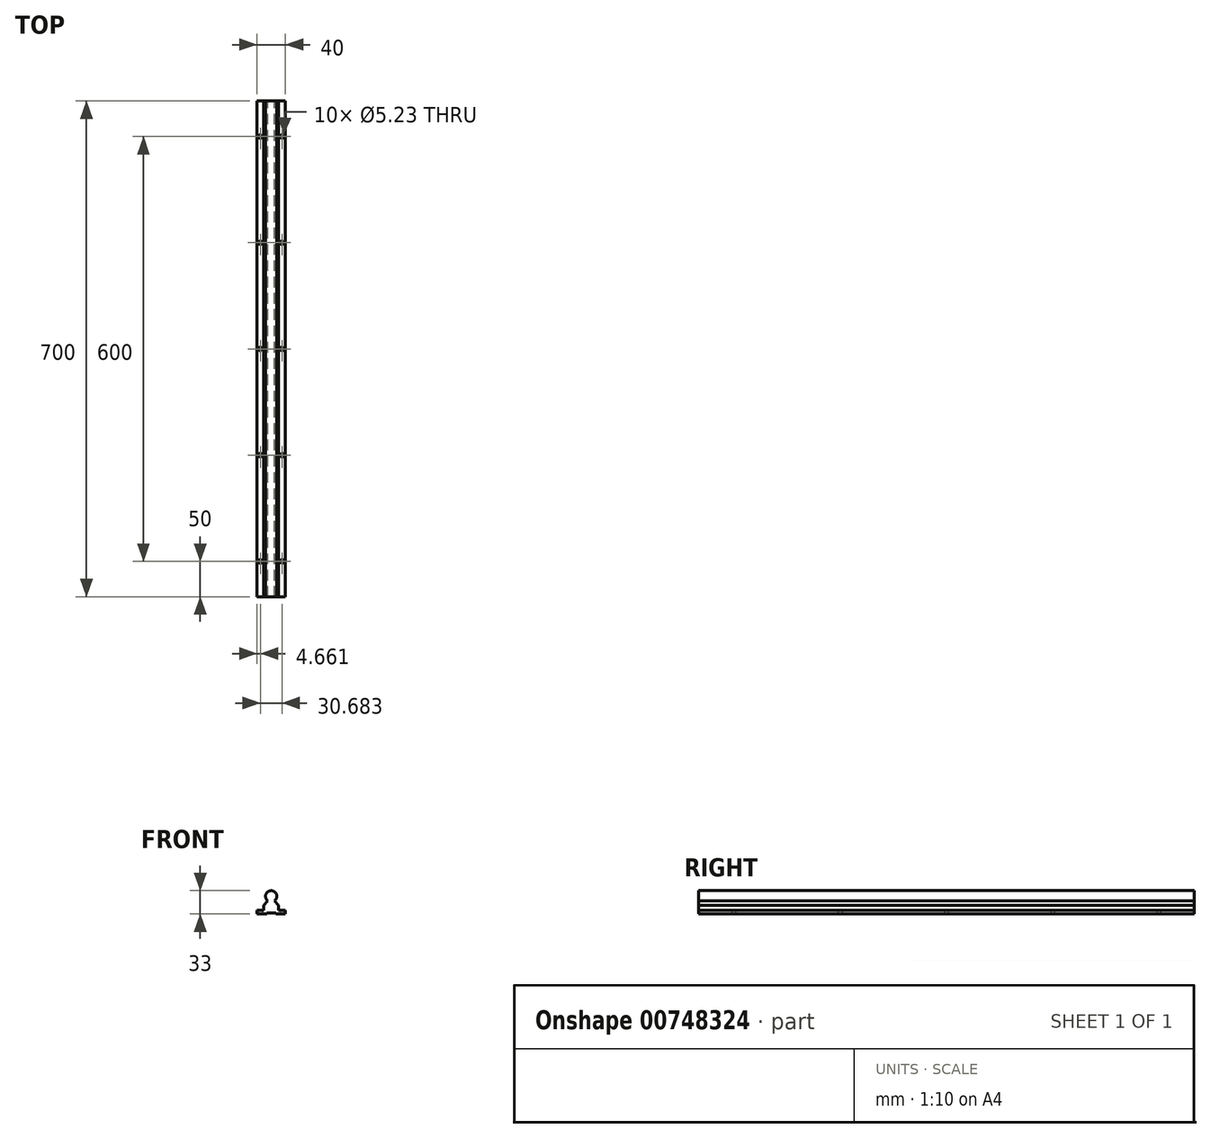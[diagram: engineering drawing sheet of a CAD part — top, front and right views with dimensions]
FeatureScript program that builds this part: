
annotation { "Feature Type Name" : "Feature", "Feature Type Description" : "" }
export const myFeature = defineFeature(function(context is Context, id is Id, definition is map)
    precondition{}
    {
        {
            var Q0;
            Q0=qCreatedBy(makeId("Front.planeOp"),FACE);
            var sketch = newSketch(context, id + "F0", { "sketchPlane" : qUnion([Q0])});
            skCircle(sketch, "E0", {"center": v(0, 0) * mm, "radius": 8 * mm});
            skLineSegment(sketch, "E1", {"start": v(0, 10.3) * mm, "end": v(0, -10.85) * mm, "construction": true});
            skLineSegment(sketch, "E2", {"start": v(12.1, 0) * mm, "end": v(-10.9, 0) * mm, "construction": true});
            skLineSegment(sketch, "E3", {"start": v(-5, -6.24) * mm, "end": v(-10.67, -13) * mm});
            skLineSegment(sketch, "E4", {"start": v(-10.67, -13) * mm, "end": v(-10.67, -20) * mm});
            skLineSegment(sketch, "E5", {"start": v(-10.67, -20) * mm, "end": v(-20, -20) * mm});
            skLineSegment(sketch, "E6", {"start": v(-20, -20) * mm, "end": v(-20, -25) * mm});
            skLineSegment(sketch, "E7", {"start": v(-20, -25) * mm, "end": v(20, -25) * mm});
            skLineSegment(sketch, "E8", {"start": v(20, -25) * mm, "end": v(20, -20) * mm});
            skLineSegment(sketch, "E9", {"start": v(20, -20) * mm, "end": v(16.54, -20) * mm});
            skLineSegment(sketch, "E10", {"start": v(10.67, -13) * mm, "end": v(5, -6.24) * mm});
            skLineSegment(sketch, "E11", {"start": v(10.67, -13) * mm, "end": v(10.67, -20) * mm});
            skLineSegment(sketch, "E12", {"start": v(10.67, -20) * mm, "end": v(16.54, -20) * mm});
            skSolve(sketch);
        }
        {
            var Q0;
            Q0=qSketchRegion(id+"F0",true);
            extrude(context, id + "F1", {"entities" : qUnion([Q0]), "depth" : 700 * mm, "offsetDistance" : 25.4 * mm});
        }
        {
            var Q0;
            Q0=makeQuery(id+"F1.opExtrude","SWEPT_FACE",FACE,{"disambiguationData":[OSD([sQuery(id+"F0.wireOp",EDGE,"E7")])]});
            var sketch = newSketch(context, id + "F2", { "sketchPlane" : qUnion([Q0])});
            skLineSegment(sketch, "E13", {"start": v(0, 700) * mm, "end": v(0, 0) * mm, "construction": true});
            skLineSegment(sketch, "E14.0", {"start": v(-6.35, 1150) * mm, "end": v(-6.35, 0) * mm, "construction": true});
            skLineSegment(sketch, "E15.0", {"start": v(6.35, 1150) * mm, "end": v(6.35, 0) * mm, "construction": true});
            skLineSegment(sketch, "E16.bottom", {"start": v(-6.35, 1150) * mm, "end": v(6.35, 1150) * mm});
            skLineSegment(sketch, "E16.top", {"start": v(-6.35, 0) * mm, "end": v(6.35, 0) * mm});
            skLineSegment(sketch, "E16.left", {"start": v(-6.35, 1150) * mm, "end": v(-6.35, 0) * mm});
            skLineSegment(sketch, "E16.right", {"start": v(6.35, 1150) * mm, "end": v(6.35, 0) * mm});
            skSolve(sketch);
        }
        {
            var Q0;
            Q0=qSketchRegion(id+"F2",true);
            extrude(context, id + "F3", {"entities" : qUnion([Q0]), "operationType" : NewBodyOperationType.REMOVE, "oppositeDirection" : true, "depth" : 1.59 * mm, "offsetDistance" : 25.4 * mm});
        }
        {
            var Q0;
            {var subQ5=sQuery(id+"F0.wireOp",EDGE,"E7");var subQ6=sQuery(id+"F0.wireOp",EDGE,"E6");Q0=makeQuery(id+"F3.boolean.opBoolean","SPLIT",FACE,{"disambiguationData":[TD([makeQuery(id+"F1.opExtrude","SWEPT_FACE",FACE,{"disambiguationData":[OSD([subQ6])]})])],"derivedFrom":makeQuery(id+"F1.opExtrude","SWEPT_FACE",FACE,{"disambiguationData":[OSD([subQ5])]})});}
            var sketch = newSketch(context, id + "F4", { "sketchPlane" : qUnion([Q0])});
            skLineSegment(sketch, "E17", {"start": v(-20, 350) * mm, "end": v(-15.34, 350) * mm, "construction": true});
            skLineSegment(sketch, "E18", {"start": v(-15.34, 350) * mm, "end": v(15.34, 350) * mm, "construction": true});
            skCircle(sketch, "E19", {"center": v(-15.34, 350) * mm, "radius": 2.62 * mm});
            skCircle(sketch, "E20", {"center": v(15.34, 350) * mm, "radius": 2.62 * mm});
            skLineSegment(sketch, "E21.0", {"start": v(-15.34, 200) * mm, "end": v(15.34, 200) * mm, "construction": true});
            skLineSegment(sketch, "E22.0", {"start": v(-15.34, 50) * mm, "end": v(15.34, 50) * mm, "construction": true});
            skLineSegment(sketch, "E23.0", {"start": v(-15.34, 500) * mm, "end": v(15.34, 500) * mm, "construction": true});
            skLineSegment(sketch, "E24.0", {"start": v(-15.34, 650) * mm, "end": v(15.34, 650) * mm, "construction": true});
            skCircle(sketch, "E25", {"center": v(15.34, 650) * mm, "radius": 2.62 * mm});
            skCircle(sketch, "E26", {"center": v(-15.34, 650) * mm, "radius": 2.62 * mm});
            skCircle(sketch, "E27", {"center": v(15.34, 500) * mm, "radius": 2.62 * mm});
            skCircle(sketch, "E28", {"center": v(-15.34, 500) * mm, "radius": 2.62 * mm});
            skCircle(sketch, "E29", {"center": v(15.34, 200) * mm, "radius": 2.62 * mm});
            skCircle(sketch, "E30", {"center": v(-15.34, 200) * mm, "radius": 2.62 * mm});
            skCircle(sketch, "E31", {"center": v(15.34, 50) * mm, "radius": 2.62 * mm});
            skCircle(sketch, "E32", {"center": v(-15.34, 50) * mm, "radius": 2.62 * mm});
            skSolve(sketch);
        }
        {
            var Q0;
            Q0 = qSketchRegion(id + "F4", true);
            extrude(context, id + "F5", {"entities" : qUnion([Q0]), "operationType" : NewBodyOperationType.REMOVE, "endBound" : BoundingType.THROUGH_ALL, "oppositeDirection" : true, "depth" : 25.4 * mm, "offsetDistance" : 25.4 * mm});
        }
    });
